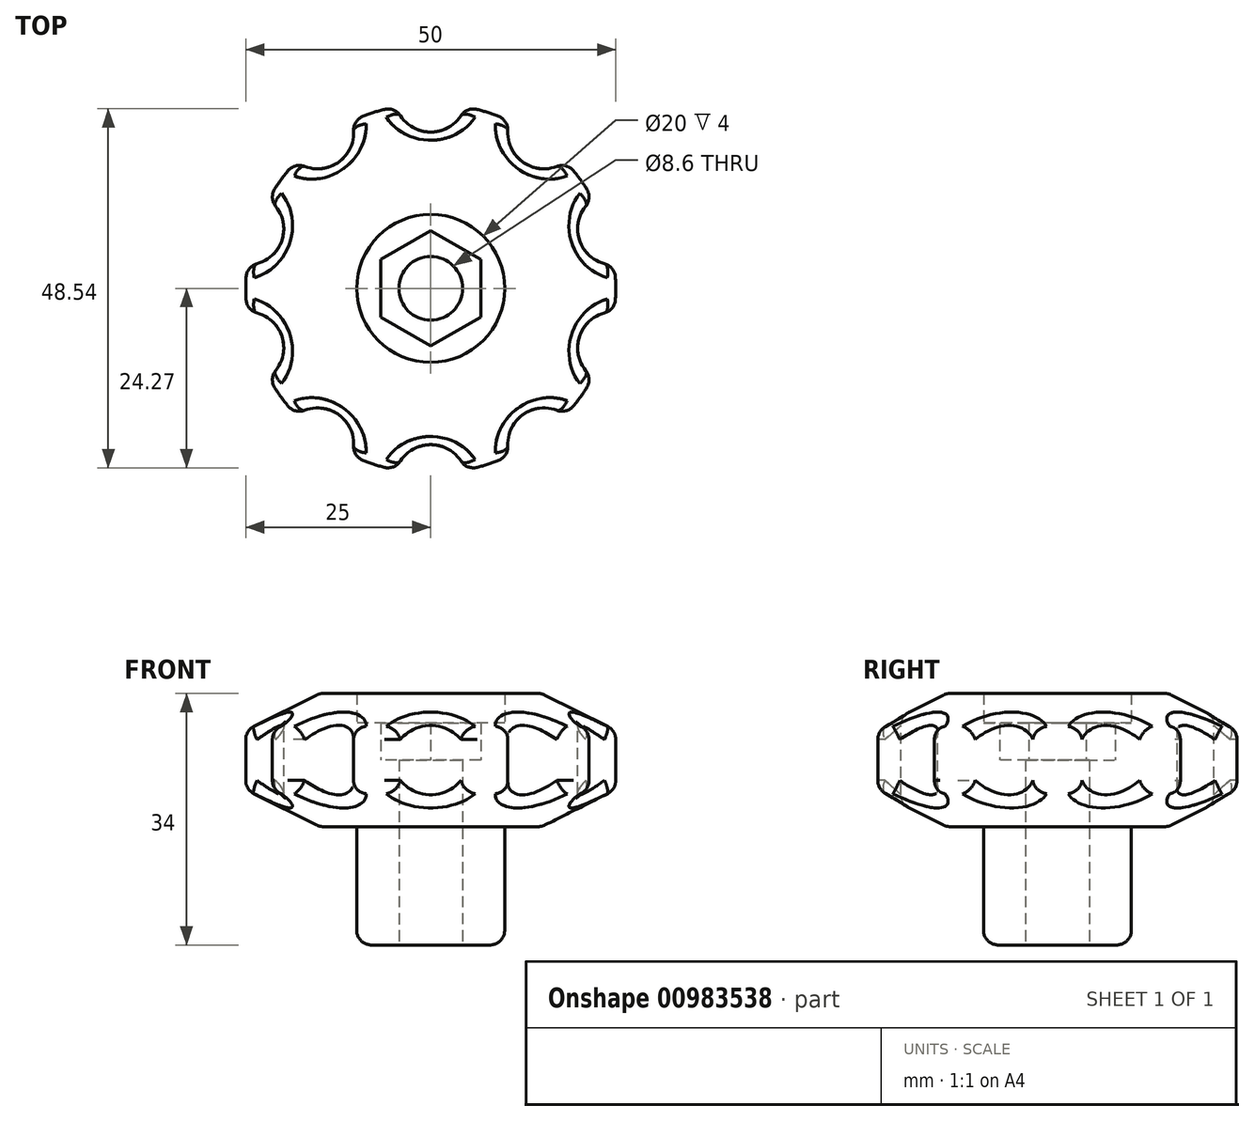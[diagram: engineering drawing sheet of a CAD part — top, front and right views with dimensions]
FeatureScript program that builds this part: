
annotation { "Feature Type Name" : "Feature", "Feature Type Description" : "" }
export const myFeature = defineFeature(function(context is Context, id is Id, definition is map)
    precondition{}
    {
        {
            var Q0;
            Q0=qCreatedBy(makeId("Top.planeOp"),FACE);
            var sketch = newSketch(context, id + "F0", { "sketchPlane" : qUnion([Q0])});
            skCircle(sketch, "E0.cCircle", {"center": v(0, 0) * mm, "radius": 6.75 * mm, "construction": true});
            skLineSegment(sketch, "E0.0", {"start": v(0, 7.8) * mm, "end": v(6.75, 3.9) * mm});
            skLineSegment(sketch, "E0.1", {"start": v(6.75, 3.9) * mm, "end": v(6.75, -3.9) * mm});
            skLineSegment(sketch, "E0.2", {"start": v(6.75, -3.9) * mm, "end": v(0, -7.8) * mm});
            skLineSegment(sketch, "E0.3", {"start": v(0, -7.8) * mm, "end": v(-6.75, -3.9) * mm});
            skLineSegment(sketch, "E0.4", {"start": v(-6.75, -3.9) * mm, "end": v(-6.75, 3.9) * mm});
            skLineSegment(sketch, "E0.5", {"start": v(-6.75, 3.9) * mm, "end": v(0, 7.8) * mm});
            skPoint(sketch, "E0.0.midPoint", {"position": v(3.37, 5.85) * mm});
            skCircle(sketch, "E1", {"center": v(0, 0) * mm, "radius": 10 * mm});
            skCircle(sketch, "E2", {"center": v(0, 0) * mm, "radius": 25 * mm});
            skSolve(sketch);
        }
        {
            var Q0;
            Q0=makeQuery(id+"F0.imprint","IMPRINT",FACE,{"disambiguationData":[TD([[makeQuery(id+"F0.imprint","IMPRINT",EDGE,{"derivedFrom":sQuery(id+"F0.wireOp",EDGE,"E0.0")}),1.0]])]});
            var Q1;
            Q1=makeQuery(id+"F0.imprint","IMPRINT",FACE,{"disambiguationData":[TD([[makeQuery(id+"F0.imprint","IMPRINT",EDGE,{"derivedFrom":sQuery(id+"F0.wireOp",EDGE,"E0.0")}),-1.0]])]});
            extrude(context, id + "F1", {"entities" : qUnion([Q0, Q1]), "oppositeDirection" : true, "depth" : 25 * mm, "offsetDistance" : 25 * mm});
        }
        {
            var Q0;
            Q0=makeQuery(id+"F0.imprint","IMPRINT",FACE,{"disambiguationData":[TD([[makeQuery(id+"F0.imprint","IMPRINT",EDGE,{"derivedFrom":sQuery(id+"F0.wireOp",EDGE,"E1")}),-1.0]])]});
            extrude(context, id + "F2", {"entities" : qUnion([Q0]), "operationType" : NewBodyOperationType.ADD, "depth" : 18 * mm, "offsetDistance" : 25 * mm, "symmetric" : true});
        }
        {
            var Q0;
            Q0=makeQuery(id+"F2.opExtrude","CAP_EDGE",EDGE,{"disambiguationData":[OSD([sQuery(id+"F0.wireOp",EDGE,"E2")])],"isStart":false});
            var Q1;
            Q1=makeQuery(id+"F2.opExtrude","SWEPT_FACE",FACE,{"disambiguationData":[OSD([sQuery(id+"F0.wireOp",EDGE,"E2")])]});
            chamfer(context, id + "F3", {"entities" : qUnion([Q0, Q1]), "chamferType" : ChamferType.TWO_OFFSETS, "width1" : 10 * mm, "oppositeDirection" : false, "width2" : 5 * mm, "tangentPropagation" : true});
        }
        {
            var Q0;
            Q0=qCreatedBy(makeId("Top.planeOp"),FACE);
            var sketch = newSketch(context, id + "F4", { "sketchPlane" : qUnion([Q0])});
            skCircle(sketch, "E3", {"center": v(0, 26) * mm, "radius": 4.87 * mm});
            skCircle(sketch, "E4.1.0", {"center": v(-15.28, 21.03) * mm, "radius": 4.87 * mm});
            skCircle(sketch, "E4.2.0", {"center": v(-24.73, 8.03) * mm, "radius": 4.87 * mm});
            skCircle(sketch, "E4.3.0", {"center": v(-24.73, -8.03) * mm, "radius": 4.87 * mm});
            skCircle(sketch, "E4.4.0", {"center": v(-15.28, -21.03) * mm, "radius": 4.87 * mm});
            skCircle(sketch, "E4.5.0", {"center": v(0, -26) * mm, "radius": 4.87 * mm});
            skCircle(sketch, "E4.6.0", {"center": v(15.28, -21.03) * mm, "radius": 4.87 * mm});
            skCircle(sketch, "E4.7.0", {"center": v(24.73, -8.03) * mm, "radius": 4.87 * mm});
            skCircle(sketch, "E4.8.0", {"center": v(24.73, 8.03) * mm, "radius": 4.87 * mm});
            skCircle(sketch, "E4.9.0", {"center": v(15.28, 21.03) * mm, "radius": 4.87 * mm});
            skPoint(sketch, "E4.center", {"position": v(0, 0) * mm});
            skSolve(sketch);
        }
        {
            var Q0;
            Q0 = qSketchRegion(id + "F4", true);
            extrude(context, id + "F5", {"entities" : qUnion([Q0]), "operationType" : NewBodyOperationType.REMOVE, "endBound" : BoundingType.THROUGH_ALL, "oppositeDirection" : true, "depth" : 25 * mm, "offsetDistance" : 25 * mm, "hasSecondDirection" : true, "secondDirectionBound" : BoundingType.THROUGH_ALL, "secondDirectionOppositeDirection" : false, "secondDirectionDepth" : 25 * mm});
        }
        {
            var Q0;
            Q0=sQuery(id+"F0.wireOp",VERTEX,"E0.cCircle.center");
            var Q1;
            Q1=makeQuery(id+"F1.opExtrude","SWEPT_BODY",BODY,{"disambiguationData":[OSD([sQuery(id+"F0.wireOp",EDGE,"E1")])]});
            hole(context, id + "F6", {"style" : HoleStyle.SIMPLE, "endStyle" : HoleEndStyle.THROUGH, "holeDiameter" : 8.6 * mm, "majorDiameter" : 5 * mm, "isTappedThrough" : true, "tappedDepth" : 12 * mm, "tapClearance" : 3, "locations" : qUnion([Q0]), "scope" : qUnion([Q1]), "startStyle" : HoleStartStyle.PART});
        }
        {
            var Q0;
            {var subQ0=sQuery(id+"F0.wireOp",EDGE,"E2");Q0=makeQuery(id+"F3.opChamfer","BLEND_FACE",FACE,{"disambiguationData":[OSD([subQ0]),TDD([makeQuery(id+"F2.opExtrude","CAP_EDGE",EDGE,{"disambiguationData":[OSD([subQ0])],"isStart":false})])]});}
            var Q1;
            Q1=makeQuery(id+"F5.boolean.opBoolean","INTERSECT",EDGE,{"disambiguationData":[OD(1.0)],"derivedFrom":[makeQuery(id+"F2.opExtrude","SWEPT_FACE",FACE,{"disambiguationData":[OSD([sQuery(id+"F0.wireOp",EDGE,"E2")])]}),makeQuery(id+"F5.opExtrude","SWEPT_FACE",FACE,{"disambiguationData":[OSD([sQuery(id+"F4.wireOp",EDGE,"E4.5.0")])]})]});
            var Q2;
            Q2=makeQuery(id+"F5.boolean.opBoolean","COPY",FACE,{"derivedFrom":makeQuery(id+"F5.opExtrude","SWEPT_FACE",FACE,{"disambiguationData":[OSD([sQuery(id+"F4.wireOp",EDGE,"E4.6.0")])]})});
            var Q3;
            Q3=makeQuery(id+"F5.boolean.opBoolean","COPY",FACE,{"derivedFrom":makeQuery(id+"F5.opExtrude","SWEPT_FACE",FACE,{"disambiguationData":[OSD([sQuery(id+"F4.wireOp",EDGE,"E4.7.0")])]})});
            var Q4;
            {var subQ0=sQuery(id+"F0.wireOp",EDGE,"E2");Q4=makeQuery(id+"F5.boolean.opBoolean","INTERSECT",EDGE,{"derivedFrom":[makeQuery(id+"F3.opChamfer","BLEND_FACE",FACE,{"disambiguationData":[OSD([subQ0]),TDD([makeQuery(id+"F2.opExtrude","CAP_EDGE",EDGE,{"disambiguationData":[OSD([subQ0])],"isStart":true})])]}),makeQuery(id+"F5.opExtrude","SWEPT_FACE",FACE,{"disambiguationData":[OSD([sQuery(id+"F4.wireOp",EDGE,"E4.8.0")])]})]});}
            var Q5;
            {var subQ0=sQuery(id+"F0.wireOp",EDGE,"E2");Q5=makeQuery(id+"F5.boolean.opBoolean","INTERSECT",EDGE,{"derivedFrom":[makeQuery(id+"F3.opChamfer","BLEND_FACE",FACE,{"disambiguationData":[OSD([subQ0]),TDD([makeQuery(id+"F2.opExtrude","CAP_EDGE",EDGE,{"disambiguationData":[OSD([subQ0])],"isStart":true})])]}),makeQuery(id+"F5.opExtrude","SWEPT_FACE",FACE,{"disambiguationData":[OSD([sQuery(id+"F4.wireOp",EDGE,"E4.9.0")])]})]});}
            var Q6;
            {var subQ0=sQuery(id+"F0.wireOp",EDGE,"E2");Q6=makeQuery(id+"F5.boolean.opBoolean","INTERSECT",EDGE,{"derivedFrom":[makeQuery(id+"F3.opChamfer","BLEND_FACE",FACE,{"disambiguationData":[OSD([subQ0]),TDD([makeQuery(id+"F2.opExtrude","CAP_EDGE",EDGE,{"disambiguationData":[OSD([subQ0])],"isStart":true})])]}),makeQuery(id+"F5.opExtrude","SWEPT_FACE",FACE,{"disambiguationData":[OSD([sQuery(id+"F4.wireOp",EDGE,"E3")])]})]});}
            var Q7;
            Q7=makeQuery(id+"F5.boolean.opBoolean","INTERSECT",EDGE,{"disambiguationData":[OD(0.0)],"derivedFrom":[makeQuery(id+"F2.opExtrude","SWEPT_FACE",FACE,{"disambiguationData":[OSD([sQuery(id+"F0.wireOp",EDGE,"E2")])]}),makeQuery(id+"F5.opExtrude","SWEPT_FACE",FACE,{"disambiguationData":[OSD([sQuery(id+"F4.wireOp",EDGE,"E4.9.0")])]})]});
            var Q8;
            Q8=makeQuery(id+"F5.boolean.opBoolean","INTERSECT",EDGE,{"disambiguationData":[OD(1.0)],"derivedFrom":[makeQuery(id+"F2.opExtrude","SWEPT_FACE",FACE,{"disambiguationData":[OSD([sQuery(id+"F0.wireOp",EDGE,"E2")])]}),makeQuery(id+"F5.opExtrude","SWEPT_FACE",FACE,{"disambiguationData":[OSD([sQuery(id+"F4.wireOp",EDGE,"E3")])]})]});
            var Q9;
            Q9=makeQuery(id+"F5.boolean.opBoolean","INTERSECT",EDGE,{"disambiguationData":[OD(1.0)],"derivedFrom":[makeQuery(id+"F2.opExtrude","SWEPT_FACE",FACE,{"disambiguationData":[OSD([sQuery(id+"F0.wireOp",EDGE,"E2")])]}),makeQuery(id+"F5.opExtrude","SWEPT_FACE",FACE,{"disambiguationData":[OSD([sQuery(id+"F4.wireOp",EDGE,"E4.9.0")])]})]});
            var Q10;
            Q10=makeQuery(id+"F5.boolean.opBoolean","INTERSECT",EDGE,{"disambiguationData":[OD(1.0)],"derivedFrom":[makeQuery(id+"F2.opExtrude","SWEPT_FACE",FACE,{"disambiguationData":[OSD([sQuery(id+"F0.wireOp",EDGE,"E2")])]}),makeQuery(id+"F5.opExtrude","SWEPT_FACE",FACE,{"disambiguationData":[OSD([sQuery(id+"F4.wireOp",EDGE,"E4.8.0")])]})]});
            var Q11;
            Q11=makeQuery(id+"F5.boolean.opBoolean","INTERSECT",EDGE,{"disambiguationData":[OD(0.0)],"derivedFrom":[makeQuery(id+"F2.opExtrude","SWEPT_FACE",FACE,{"disambiguationData":[OSD([sQuery(id+"F0.wireOp",EDGE,"E2")])]}),makeQuery(id+"F5.opExtrude","SWEPT_FACE",FACE,{"disambiguationData":[OSD([sQuery(id+"F4.wireOp",EDGE,"E3")])]})]});
            var Q12;
            Q12=makeQuery(id+"F5.boolean.opBoolean","COPY",FACE,{"derivedFrom":makeQuery(id+"F5.opExtrude","SWEPT_FACE",FACE,{"disambiguationData":[OSD([sQuery(id+"F4.wireOp",EDGE,"E4.1.0")])]})});
            var Q13;
            {var subQ0=sQuery(id+"F0.wireOp",EDGE,"E2");var subQ1=makeQuery(id+"F2.opExtrude","SWEPT_FACE",FACE,{"disambiguationData":[OSD([subQ0])]});var subQ2=makeQuery(id+"F2.opExtrude","CAP_EDGE",EDGE,{"disambiguationData":[OSD([subQ0])],"isStart":true});Q13=makeQuery(id+"F5.boolean.opBoolean","SPLIT",EDGE,{"disambiguationData":[TD([subQ1,makeQuery(id+"F3.opChamfer","BLEND_FACE",FACE,{"disambiguationData":[OSD([subQ0]),TDD([subQ2])]}),makeQuery(id+"F5.opExtrude","SWEPT_FACE",FACE,{"disambiguationData":[OSD([sQuery(id+"F4.wireOp",EDGE,"E3")])]}),makeQuery(id+"F5.opExtrude","SWEPT_FACE",FACE,{"disambiguationData":[OSD([sQuery(id+"F4.wireOp",EDGE,"E4.1.0")])]})])],"derivedFrom":makeQuery(id+"F3.opChamfer","BLEND_EDGE",EDGE,{"blendedFrom":[subQ2,subQ1],"blendedInto":[subQ1]})});}
            var Q14;
            Q14=makeQuery(id+"F5.boolean.opBoolean","INTERSECT",EDGE,{"disambiguationData":[OD(0.0)],"derivedFrom":[makeQuery(id+"F2.opExtrude","SWEPT_FACE",FACE,{"disambiguationData":[OSD([sQuery(id+"F0.wireOp",EDGE,"E2")])]}),makeQuery(id+"F5.opExtrude","SWEPT_FACE",FACE,{"disambiguationData":[OSD([sQuery(id+"F4.wireOp",EDGE,"E4.8.0")])]})]});
            var Q15;
            {var subQ0=sQuery(id+"F0.wireOp",EDGE,"E2");Q15=makeQuery(id+"F5.boolean.opBoolean","INTERSECT",EDGE,{"derivedFrom":[makeQuery(id+"F3.opChamfer","BLEND_FACE",FACE,{"disambiguationData":[OSD([subQ0]),TDD([makeQuery(id+"F2.opExtrude","CAP_EDGE",EDGE,{"disambiguationData":[OSD([subQ0])],"isStart":true})])]}),makeQuery(id+"F5.opExtrude","SWEPT_FACE",FACE,{"disambiguationData":[OSD([sQuery(id+"F4.wireOp",EDGE,"E4.2.0")])]})]});}
            var Q16;
            Q16=makeQuery(id+"F5.boolean.opBoolean","INTERSECT",EDGE,{"disambiguationData":[OD(0.0)],"derivedFrom":[makeQuery(id+"F2.opExtrude","SWEPT_FACE",FACE,{"disambiguationData":[OSD([sQuery(id+"F0.wireOp",EDGE,"E2")])]}),makeQuery(id+"F5.opExtrude","SWEPT_FACE",FACE,{"disambiguationData":[OSD([sQuery(id+"F4.wireOp",EDGE,"E4.2.0")])]})]});
            var Q17;
            Q17=makeQuery(id+"F5.boolean.opBoolean","INTERSECT",EDGE,{"disambiguationData":[OD(1.0)],"derivedFrom":[makeQuery(id+"F2.opExtrude","SWEPT_FACE",FACE,{"disambiguationData":[OSD([sQuery(id+"F0.wireOp",EDGE,"E2")])]}),makeQuery(id+"F5.opExtrude","SWEPT_FACE",FACE,{"disambiguationData":[OSD([sQuery(id+"F4.wireOp",EDGE,"E4.2.0")])]})]});
            var Q18;
            {var subQ0=sQuery(id+"F0.wireOp",EDGE,"E2");Q18=makeQuery(id+"F5.boolean.opBoolean","INTERSECT",EDGE,{"derivedFrom":[makeQuery(id+"F3.opChamfer","BLEND_FACE",FACE,{"disambiguationData":[OSD([subQ0]),TDD([makeQuery(id+"F2.opExtrude","CAP_EDGE",EDGE,{"disambiguationData":[OSD([subQ0])],"isStart":true})])]}),makeQuery(id+"F5.opExtrude","SWEPT_FACE",FACE,{"disambiguationData":[OSD([sQuery(id+"F4.wireOp",EDGE,"E4.3.0")])]})]});}
            var Q19;
            {var subQ0=sQuery(id+"F0.wireOp",EDGE,"E2");var subQ1=makeQuery(id+"F2.opExtrude","SWEPT_FACE",FACE,{"disambiguationData":[OSD([subQ0])]});var subQ2=makeQuery(id+"F2.opExtrude","CAP_EDGE",EDGE,{"disambiguationData":[OSD([subQ0])],"isStart":true});Q19=makeQuery(id+"F5.boolean.opBoolean","SPLIT",EDGE,{"disambiguationData":[TD([subQ1,makeQuery(id+"F3.opChamfer","BLEND_FACE",FACE,{"disambiguationData":[OSD([subQ0]),TDD([subQ2])]}),makeQuery(id+"F5.opExtrude","SWEPT_FACE",FACE,{"disambiguationData":[OSD([sQuery(id+"F4.wireOp",EDGE,"E4.2.0")])]}),makeQuery(id+"F5.opExtrude","SWEPT_FACE",FACE,{"disambiguationData":[OSD([sQuery(id+"F4.wireOp",EDGE,"E4.3.0")])]})])],"derivedFrom":makeQuery(id+"F3.opChamfer","BLEND_EDGE",EDGE,{"blendedFrom":[subQ2,subQ1],"blendedInto":[subQ1]})});}
            var Q20;
            {var subQ0=sQuery(id+"F0.wireOp",EDGE,"E2");Q20=makeQuery(id+"F3.opChamfer","BLEND_FACE",FACE,{"disambiguationData":[OSD([subQ0]),TDD([makeQuery(id+"F2.opExtrude","CAP_EDGE",EDGE,{"disambiguationData":[OSD([subQ0])],"isStart":true})])]});}
            var Q21;
            Q21=makeQuery(id+"F5.boolean.opBoolean","INTERSECT",EDGE,{"disambiguationData":[OD(0.0)],"derivedFrom":[makeQuery(id+"F2.opExtrude","SWEPT_FACE",FACE,{"disambiguationData":[OSD([sQuery(id+"F0.wireOp",EDGE,"E2")])]}),makeQuery(id+"F5.opExtrude","SWEPT_FACE",FACE,{"disambiguationData":[OSD([sQuery(id+"F4.wireOp",EDGE,"E4.3.0")])]})]});
            var Q22;
            Q22=makeQuery(id+"F5.boolean.opBoolean","INTERSECT",EDGE,{"disambiguationData":[OD(1.0)],"derivedFrom":[makeQuery(id+"F2.opExtrude","SWEPT_FACE",FACE,{"disambiguationData":[OSD([sQuery(id+"F0.wireOp",EDGE,"E2")])]}),makeQuery(id+"F5.opExtrude","SWEPT_FACE",FACE,{"disambiguationData":[OSD([sQuery(id+"F4.wireOp",EDGE,"E4.3.0")])]})]});
            var Q23;
            Q23=makeQuery(id+"F5.boolean.opBoolean","INTERSECT",EDGE,{"disambiguationData":[OD(0.0)],"derivedFrom":[makeQuery(id+"F2.opExtrude","SWEPT_FACE",FACE,{"disambiguationData":[OSD([sQuery(id+"F0.wireOp",EDGE,"E2")])]}),makeQuery(id+"F5.opExtrude","SWEPT_FACE",FACE,{"disambiguationData":[OSD([sQuery(id+"F4.wireOp",EDGE,"E4.4.0")])]})]});
            var Q24;
            Q24=makeQuery(id+"F5.boolean.opBoolean","INTERSECT",EDGE,{"disambiguationData":[OD(1.0)],"derivedFrom":[makeQuery(id+"F2.opExtrude","SWEPT_FACE",FACE,{"disambiguationData":[OSD([sQuery(id+"F0.wireOp",EDGE,"E2")])]}),makeQuery(id+"F5.opExtrude","SWEPT_FACE",FACE,{"disambiguationData":[OSD([sQuery(id+"F4.wireOp",EDGE,"E4.4.0")])]})]});
            var Q25;
            Q25=makeQuery(id+"F5.boolean.opBoolean","INTERSECT",EDGE,{"disambiguationData":[OD(0.0)],"derivedFrom":[makeQuery(id+"F2.opExtrude","SWEPT_FACE",FACE,{"disambiguationData":[OSD([sQuery(id+"F0.wireOp",EDGE,"E2")])]}),makeQuery(id+"F5.opExtrude","SWEPT_FACE",FACE,{"disambiguationData":[OSD([sQuery(id+"F4.wireOp",EDGE,"E4.5.0")])]})]});
            fillet(context, id + "F7", {"entities" : qUnion([Q0, Q1, Q2, Q3, Q4, Q5, Q6, Q7, Q8, Q9, Q10, Q11, Q12, Q13, Q14, Q15, Q16, Q17, Q18, Q19, Q20, Q21, Q22, Q23, Q24, Q25]), "radius" : 2 * mm, "tangentPropagation" : true, "allowEdgeOverflow" : false});
        }
        {
            var Q0;
            Q0=makeQuery(id+"F0.imprint","IMPRINT",FACE,{"disambiguationData":[TD([[makeQuery(id+"F0.imprint","IMPRINT",EDGE,{"derivedFrom":sQuery(id+"F0.wireOp",EDGE,"E0.0")}),1.0]])]});
            extrude(context, id + "F8", {"entities" : qUnion([Q0]), "operationType" : NewBodyOperationType.ADD, "depth" : 10 * mm, "offsetDistance" : 25 * mm, "symmetric" : true});
        }
        {
            var Q0;
            Q0=makeQuery(id+"F1.opExtrude","CAP_EDGE",EDGE,{"disambiguationData":[OSD([sQuery(id+"F0.wireOp",EDGE,"E1")])],"isStart":false});
            var Q1;
            Q1=makeQuery(id+"F2.opExtrude","CAP_EDGE",EDGE,{"disambiguationData":[OSD([sQuery(id+"F0.wireOp",EDGE,"E1")])],"isStart":true});
            fillet(context, id + "F9", {"entities" : qUnion([Q0, Q1]), "radius" : 2 * mm, "tangentPropagation" : true, "allowEdgeOverflow" : false});
        }
    });
